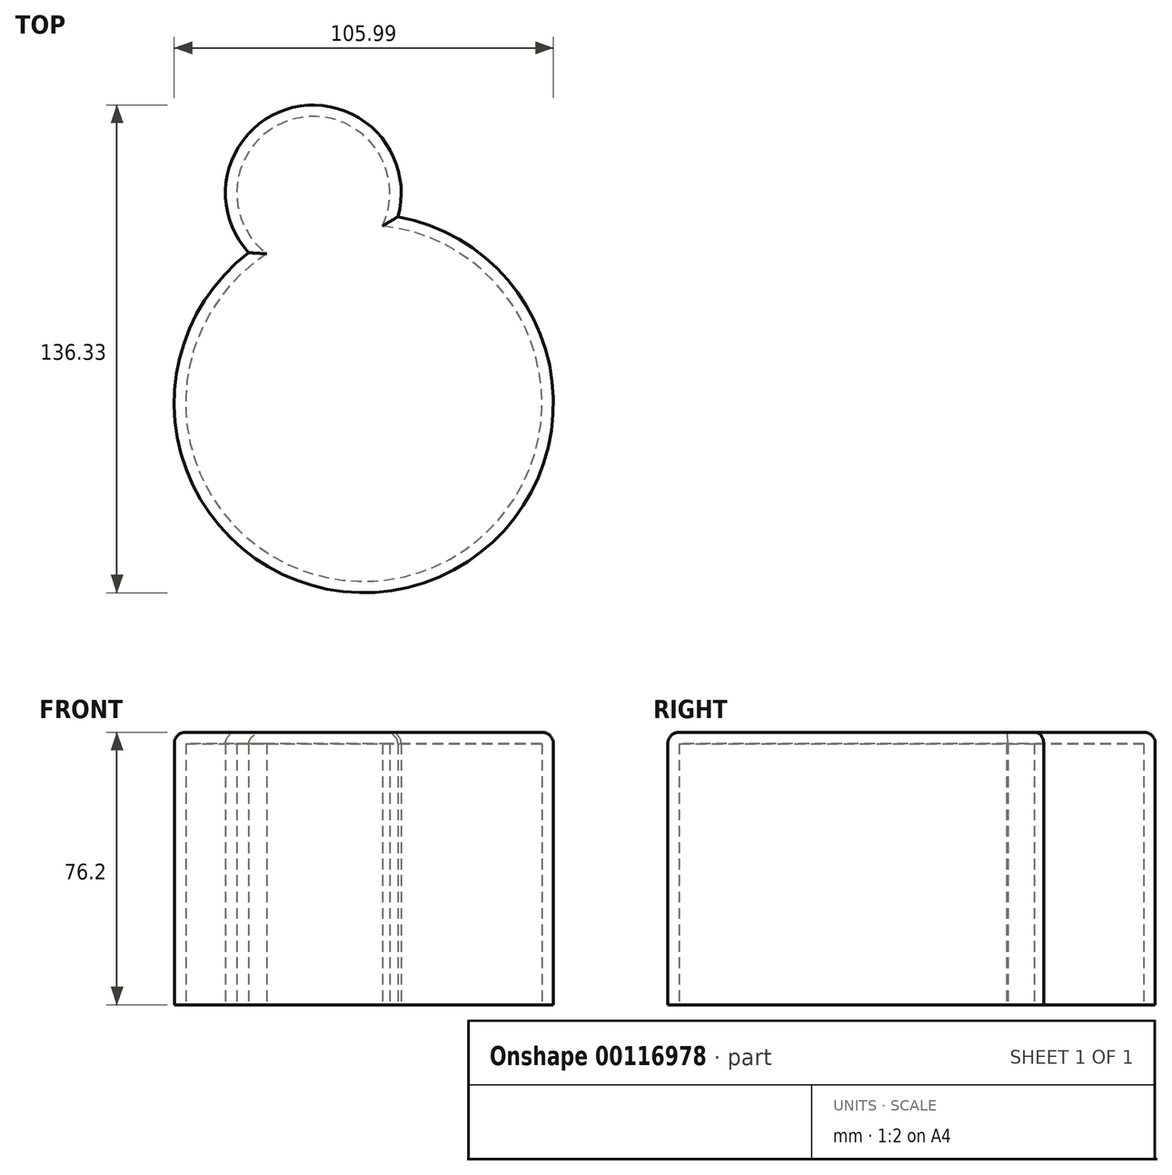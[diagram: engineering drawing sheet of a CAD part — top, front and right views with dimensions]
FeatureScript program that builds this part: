
annotation { "Feature Type Name" : "Feature", "Feature Type Description" : "" }
export const myFeature = defineFeature(function(context is Context, id is Id, definition is map)
    precondition{}
    {
        {
            var Q0;
            Q0=qCreatedBy(makeId("Top.planeOp"),FACE);
            var sketch = newSketch(context, id + "F0", { "sketchPlane" : qUnion([Q0])});
            skArc(sketch, "E0", {"start": v(-89.56, -6.64) * mm, "mid": v(-118.96, 23.9) * mm, "end": v(-131.28, -16.66) * mm});
            skArc(sketch, "E1", {"start": v(-131.28, -16.66) * mm, "mid": v(-86.72, -110.3) * mm, "end": v(-89.56, -6.64) * mm});
            skSolve(sketch);
        }
        {
            var Q0;
            Q0=makeQuery(id+"F0.imprint","IMPRINT",FACE,{"disambiguationData":[TD([[makeQuery(id+"F0.imprint","IMPRINT",EDGE,{"derivedFrom":sQuery(id+"F0.wireOp",EDGE,"E0")}),1.0]])]});
            extrude(context, id + "F1", {"entities" : qUnion([Q0]), "depth" : 76.2 * mm});
        }
        {
            var Q0;
            Q0=makeQuery(id+"F1.opExtrude","CAP_EDGE",EDGE,{"disambiguationData":[OSD([sQuery(id+"F0.wireOp",EDGE,"E1")])],"isStart":false});
            var Q1;
            Q1=makeQuery(id+"F1.opExtrude","CAP_EDGE",EDGE,{"disambiguationData":[OSD([sQuery(id+"F0.wireOp",EDGE,"E0")])],"isStart":false});
            fillet(context, id + "F2", {"entities" : qUnion([Q0, Q1]), "radius" : 3.17 * mm, "tangentPropagation" : true, "allowEdgeOverflow" : false});
        }
        {
            var Q0;
            Q0=makeQuery(id+"F1.opExtrude","CAP_FACE",FACE,{"disambiguationData":[OSD([sQuery(id+"F0.wireOp",EDGE,"E0"),sQuery(id+"F0.wireOp",EDGE,"E1")])],"isStart":true});
            shell(context, id + "F3", {"entities" : qUnion([Q0]), "thickness" : 3.17 * mm});
        }
    });
